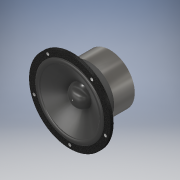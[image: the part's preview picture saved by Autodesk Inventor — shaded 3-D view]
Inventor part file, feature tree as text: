
AUTODESK INVENTOR PART (.ipt)
format: ipt  version: 2019 (Build 230136000, 136)  size: 218,112 bytes
history: native  units: mm
features: sketch x9, extrude x8, fillet x3, other x2, projected_geometry x2, hole x1, loft x1, chamfer x1
ambient origin geometry x8: Origin, YZ Plane, XZ Plane, XY Plane, X Axis, Y Axis, Z Axis, Center Point
bodies: Solid1 (feature_tree)
feature tree (27):
  extrude  "Extrusion1"  Depth=5.5mm TaperAngle=0.0deg
  hole  "Hole1"  [1 undecoded]
  extrude  "Extrusion2"  Depth=125.0mm
  extrude  "Extrusion3"  Depth=5.0mm
  loft  "Loft1"
  extrude  "Extrusion4"  Depth=90.0mm
  extrude  "Extrusion5"  Depth=2.5mm
  fillet  "Fillet1"  Radius=2.5mm
  extrude  "Extrusion6"  Depth=3.0mm
  fillet  "Fillet2"  Radius=9.0mm
  extrude  "Extrusion7"  Depth=6.0mm
  chamfer  "Chamfer1"  Distance=40.0mm
  extrude  "Extrusion8"  Depth=25.0mm TaperAngle=0.0deg
  fillet  "Fillet3"  Radius=33.5mm
  sketch  "Sketch1"  dims[d0=148.0mm d1=5.5mm d2=0.0mm]
  sketch  "Sketch2"  dims[d3=136.0mm d4=50.0mm d6=360.0deg]
  sketch  "Sketch3"  dims[d8=5.3mm d9=9.525mm d10=4.0mm d11=2.0mm d12=90.0deg d13=19.05mm d14=20.594885mm d15=125.0mm]
  sketch  "Sketch4"  dims[d16=5.0mm d17=0.0mm d18=90.0mm]
  other  "Edges1"
  other  "Edges2"
  sketch  "Sketch5"  dims[d19=25.0mm d20=0.0mm d21=0.0mm d22=90.0deg]
  sketch  "Sketch6"  dims[d23=0.0mm d24=90.0deg d25=90.0mm]
  projected_geometry  "Projected Loop1"
  sketch  "Sketch7"  dims[d26=37.5mm d27=0.0mm d28=55.0mm d31=2.5mm d32=0.0mm]
  sketch  "Sketch8"  dims[d33=3.0mm d34=125.0mm d35=9.0mm]
  sketch  "Sketch9"  dims[d36=2.5mm d37=0.0mm d38=6.0mm d39=40.0mm d40=25.0mm d41=0.0mm d42=33.5mm d43=2.0mm d44=30.0deg d45=20.0mm d46=0.0mm d47=20.0mm d48=0.0mm]
  projected_geometry  "Projected Loop2"
note: 1 required parameter value undecoded (feature->parameter linkage not recoverable at this tier; creation-order binding heuristic only, values carry confidence <= 0.55)
